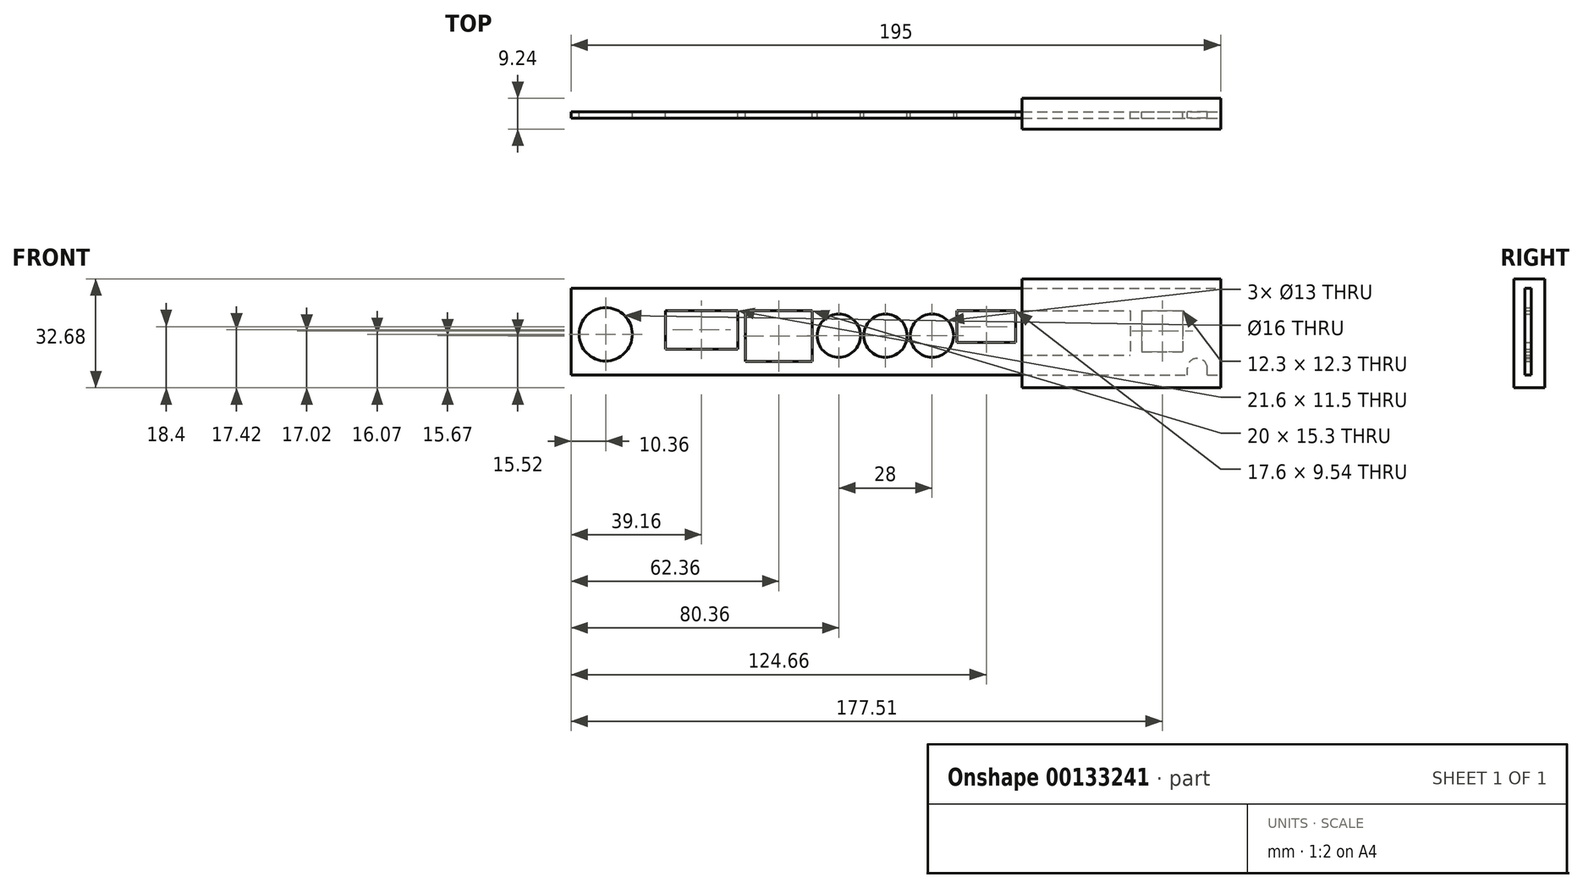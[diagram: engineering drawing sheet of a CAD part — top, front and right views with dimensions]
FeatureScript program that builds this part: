
annotation { "Feature Type Name" : "Feature", "Feature Type Description" : "" }
export const myFeature = defineFeature(function(context is Context, id is Id, definition is map)
    precondition{}
    {
        {
            var Q0;
            Q0=qCreatedBy(makeId("Front.planeOp"),FACE);
            var sketch = newSketch(context, id + "F0", { "sketchPlane" : qUnion([Q0])});
            skLineSegment(sketch, "E0.bottom", {"start": v(-97.5, 0) * mm, "end": v(97.5, 0) * mm});
            skLineSegment(sketch, "E0.top", {"start": v(-97.5, -26) * mm, "end": v(87.5, -26) * mm});
            skLineSegment(sketch, "E0.left", {"start": v(-97.5, 0) * mm, "end": v(-97.5, -26) * mm});
            skLineSegment(sketch, "E0.right", {"start": v(97.5, 0) * mm, "end": v(97.5, -26) * mm});
            skPoint(sketch, "E1", {"position": v(0, 0) * mm});
            skLineSegment(sketch, "E2", {"start": v(-87.14, -4.04) * mm, "end": v(-87.14, -25.05) * mm, "construction": true});
            skLineSegment(sketch, "E3", {"start": v(-100.2, -13.8) * mm, "end": v(-77.18, -13.8) * mm, "construction": true});
            skCircle(sketch, "E4", {"center": v(-87.14, -13.8) * mm, "radius": 8 * mm});
            skLineSegment(sketch, "E5.bottom", {"start": v(-69.14, -6.7) * mm, "end": v(-47.54, -6.7) * mm});
            skLineSegment(sketch, "E5.top", {"start": v(-69.14, -18.2) * mm, "end": v(-47.54, -18.2) * mm});
            skLineSegment(sketch, "E5.left", {"start": v(-69.14, -6.7) * mm, "end": v(-69.14, -18.2) * mm});
            skLineSegment(sketch, "E5.right", {"start": v(-47.54, -6.7) * mm, "end": v(-47.54, -18.2) * mm});
            skLineSegment(sketch, "E6.bottom", {"start": v(-45.14, -6.7) * mm, "end": v(-25.14, -6.7) * mm});
            skLineSegment(sketch, "E6.top", {"start": v(-45.14, -22) * mm, "end": v(-25.14, -22) * mm});
            skLineSegment(sketch, "E6.left", {"start": v(-45.14, -6.7) * mm, "end": v(-45.14, -22) * mm});
            skLineSegment(sketch, "E6.right", {"start": v(-25.14, -6.7) * mm, "end": v(-25.14, -22) * mm});
            skCircle(sketch, "E7", {"center": v(-17.14, -14.2) * mm, "radius": 6.5 * mm});
            skCircle(sketch, "E8.1.0.0", {"center": v(-3.14, -14.2) * mm, "radius": 6.5 * mm});
            skCircle(sketch, "E8.2.0.0", {"center": v(10.86, -14.2) * mm, "radius": 6.5 * mm});
            skLineSegment(sketch, "E8.direction1", {"start": v(-17.14, -14.2) * mm, "end": v(-3.14, -14.2) * mm, "construction": true});
            skLineSegment(sketch, "E9.bottom", {"start": v(18.36, -6.7) * mm, "end": v(35.96, -6.7) * mm});
            skLineSegment(sketch, "E9.top", {"start": v(18.36, -16.24) * mm, "end": v(35.96, -16.24) * mm});
            skLineSegment(sketch, "E9.left", {"start": v(18.36, -6.7) * mm, "end": v(18.36, -16.24) * mm});
            skLineSegment(sketch, "E9.right", {"start": v(35.96, -6.7) * mm, "end": v(35.96, -16.24) * mm});
            skLineSegment(sketch, "E10.bottom", {"start": v(37.86, -6.7) * mm, "end": v(70.36, -6.7) * mm});
            skLineSegment(sketch, "E10.top", {"start": v(37.86, -20.1) * mm, "end": v(70.36, -20.1) * mm});
            skLineSegment(sketch, "E10.left", {"start": v(37.86, -6.7) * mm, "end": v(37.86, -20.1) * mm});
            skLineSegment(sketch, "E10.right", {"start": v(70.36, -6.7) * mm, "end": v(70.36, -20.1) * mm});
            skLineSegment(sketch, "E11.bottom", {"start": v(73.86, -6.7) * mm, "end": v(86.16, -6.7) * mm});
            skLineSegment(sketch, "E11.top", {"start": v(73.86, -19) * mm, "end": v(86.16, -19) * mm});
            skLineSegment(sketch, "E11.left", {"start": v(73.86, -6.7) * mm, "end": v(73.86, -19) * mm});
            skLineSegment(sketch, "E11.right", {"start": v(86.16, -6.7) * mm, "end": v(86.16, -19) * mm});
            skLineSegment(sketch, "E12.top", {"start": v(90.5, -21) * mm, "end": v(90.5, -21) * mm});
            skLineSegment(sketch, "E12.left", {"start": v(87.5, -26) * mm, "end": v(87.5, -24) * mm});
            skLineSegment(sketch, "E12.right", {"start": v(93.5, -26) * mm, "end": v(93.5, -24) * mm});
            skPoint(sketch, "E13.visualSharp", {"position": v(87.5, -21) * mm});
            skArc(sketch, "E13.filletArc", {"start": v(90.5, -21) * mm, "mid": v(88.38, -21.88) * mm, "end": v(87.5, -24) * mm});
            skPoint(sketch, "E14.visualSharp", {"position": v(93.5, -21) * mm});
            skArc(sketch, "E14.filletArc", {"start": v(93.5, -24) * mm, "mid": v(92.62, -21.88) * mm, "end": v(90.5, -21) * mm});
            skLineSegment(sketch, "E15.trimOffspring", {"start": v(93.5, -26) * mm, "end": v(97.5, -26) * mm});
            skSolve(sketch);
        }
        {
            var Q0;
            Q0=makeQuery(id+"F0.imprint","IMPRINT",FACE,{"disambiguationData":[TD([[makeQuery(id+"F0.imprint","IMPRINT",EDGE,{"derivedFrom":sQuery(id+"F0.wireOp",EDGE,"E0.bottom")}),-1.0]])]});
            extrude(context, id + "F1", {"entities" : qUnion([Q0]), "depth" : 2 * mm});
        }
        {
            var Q0;
            Q0=makeQuery(id+"F1.opExtrude","SWEPT_FACE",FACE,{"disambiguationData":[OSD([sQuery(id+"F0.wireOp",EDGE,"E10.left")])]});
            cPlane(context, id + "F2", {"entities" : qUnion([Q0]), "cplaneType" : CPlaneType.OFFSET, "offset" : 0 * mm, "width" : 150 * mm, "height" : 150 * mm});
        }
        {
            var Q0;
            Q0=qCreatedBy(id+"F2.planeOp",FACE);
            var sketch = newSketch(context, id + "F3", { "sketchPlane" : qUnion([Q0])});
            skLineSegment(sketch, "E16.bottom", {"start": v(-5.21, -29.87) * mm, "end": v(4.03, -29.87) * mm});
            skLineSegment(sketch, "E16.top", {"start": v(-5.21, 2.8) * mm, "end": v(4.03, 2.8) * mm});
            skLineSegment(sketch, "E16.left", {"start": v(-5.21, -29.87) * mm, "end": v(-5.21, 2.8) * mm});
            skLineSegment(sketch, "E16.right", {"start": v(4.03, -29.87) * mm, "end": v(4.03, 2.8) * mm});
            skSolve(sketch);
        }
        {
            var Q0;
            Q0 = qSketchRegion(id + "F3", true);
            var Q1;
            Q1=makeQuery(id+"F1.opExtrude","SWEPT_FACE",FACE,{"disambiguationData":[OSD([sQuery(id+"F0.wireOp",EDGE,"E0.right")])]});
            extrude(context, id + "F4", {"entities" : qUnion([Q0]), "endBound" : BoundingType.UP_TO_SURFACE, "endBoundEntityFace" : qUnion([Q1]), "depth" : 39.23 * mm});
        }
        {
            var Q0;
            Q0=makeQuery(id+"F4.opExtrude","CAP_FACE",FACE,{"disambiguationData":[OSD([sQuery(id+"F3.wireOp",EDGE,"E16.bottom"),sQuery(id+"F3.wireOp",EDGE,"E16.top"),sQuery(id+"F3.wireOp",EDGE,"E16.left"),sQuery(id+"F3.wireOp",EDGE,"E16.right")])],"isStart":true});
            var Q1;
            Q1=makeQuery(id+"F1.opExtrude","SWEPT_FACE",FACE,{"disambiguationData":[OSD([sQuery(id+"F0.wireOp",EDGE,"E0.left")])]});
            extrude(context, id + "F5", {"entities" : qUnion([Q0]), "endBound" : BoundingType.UP_TO_SURFACE, "endBoundEntityFace" : qUnion([Q1]), "depth" : 25 * mm});
        }
        {
            var Q0;
            Q0=makeQuery(id+"F1.opExtrude","SWEPT_BODY",BODY,{"disambiguationData":[OSD([sQuery(id+"F0.wireOp",EDGE,"E0.bottom"),sQuery(id+"F0.wireOp",EDGE,"E0.top"),sQuery(id+"F0.wireOp",EDGE,"E0.left"),sQuery(id+"F0.wireOp",EDGE,"E0.right"),sQuery(id+"F0.wireOp",EDGE,"E4"),sQuery(id+"F0.wireOp",EDGE,"E5.bottom"),sQuery(id+"F0.wireOp",EDGE,"E5.top"),sQuery(id+"F0.wireOp",EDGE,"E5.left"),sQuery(id+"F0.wireOp",EDGE,"E5.right"),sQuery(id+"F0.wireOp",EDGE,"E6.bottom"),sQuery(id+"F0.wireOp",EDGE,"E6.top"),sQuery(id+"F0.wireOp",EDGE,"E6.left"),sQuery(id+"F0.wireOp",EDGE,"E6.right"),sQuery(id+"F0.wireOp",EDGE,"E7"),sQuery(id+"F0.wireOp",EDGE,"E8.1.0.0"),sQuery(id+"F0.wireOp",EDGE,"E8.2.0.0"),sQuery(id+"F0.wireOp",EDGE,"E9.bottom"),sQuery(id+"F0.wireOp",EDGE,"E9.top"),sQuery(id+"F0.wireOp",EDGE,"E9.left"),sQuery(id+"F0.wireOp",EDGE,"E9.right"),sQuery(id+"F0.wireOp",EDGE,"E10.bottom"),sQuery(id+"F0.wireOp",EDGE,"E10.top"),sQuery(id+"F0.wireOp",EDGE,"E10.left"),sQuery(id+"F0.wireOp",EDGE,"E10.right"),sQuery(id+"F0.wireOp",EDGE,"E11.bottom"),sQuery(id+"F0.wireOp",EDGE,"E11.top"),sQuery(id+"F0.wireOp",EDGE,"E11.left"),sQuery(id+"F0.wireOp",EDGE,"E11.right")])]});
            var Q1;
            Q1=makeQuery(id+"F4.opExtrude","SWEPT_BODY",BODY,{"disambiguationData":[OSD([sQuery(id+"F3.wireOp",EDGE,"E16.bottom"),sQuery(id+"F3.wireOp",EDGE,"E16.top"),sQuery(id+"F3.wireOp",EDGE,"E16.left"),sQuery(id+"F3.wireOp",EDGE,"E16.right")])]});
            booleanBodies(context, id + "F6", {"operationType" : BooleanOperationType.INTERSECTION, "tools" : qUnion([Q0, Q1]), "keepTools" : true});
        }
        {
            var Q0;
            Q0=makeQuery(id+"F5.opExtrude","SWEPT_BODY",BODY,{"disambiguationData":[OSD([sQuery(id+"F3.wireOp",EDGE,"E16.bottom"),sQuery(id+"F3.wireOp",EDGE,"E16.top"),sQuery(id+"F3.wireOp",EDGE,"E16.left"),sQuery(id+"F3.wireOp",EDGE,"E16.right")])]});
            var Q1;
            Q1=makeQuery(id+"F1.opExtrude","SWEPT_BODY",BODY,{"disambiguationData":[OSD([sQuery(id+"F0.wireOp",EDGE,"E0.bottom"),sQuery(id+"F0.wireOp",EDGE,"E0.top"),sQuery(id+"F0.wireOp",EDGE,"E0.left"),sQuery(id+"F0.wireOp",EDGE,"E0.right"),sQuery(id+"F0.wireOp",EDGE,"E4"),sQuery(id+"F0.wireOp",EDGE,"E5.bottom"),sQuery(id+"F0.wireOp",EDGE,"E5.top"),sQuery(id+"F0.wireOp",EDGE,"E5.left"),sQuery(id+"F0.wireOp",EDGE,"E5.right"),sQuery(id+"F0.wireOp",EDGE,"E6.bottom"),sQuery(id+"F0.wireOp",EDGE,"E6.top"),sQuery(id+"F0.wireOp",EDGE,"E6.left"),sQuery(id+"F0.wireOp",EDGE,"E6.right"),sQuery(id+"F0.wireOp",EDGE,"E7"),sQuery(id+"F0.wireOp",EDGE,"E8.1.0.0"),sQuery(id+"F0.wireOp",EDGE,"E8.2.0.0"),sQuery(id+"F0.wireOp",EDGE,"E9.bottom"),sQuery(id+"F0.wireOp",EDGE,"E9.top"),sQuery(id+"F0.wireOp",EDGE,"E9.left"),sQuery(id+"F0.wireOp",EDGE,"E9.right"),sQuery(id+"F0.wireOp",EDGE,"E10.bottom"),sQuery(id+"F0.wireOp",EDGE,"E10.top"),sQuery(id+"F0.wireOp",EDGE,"E10.left"),sQuery(id+"F0.wireOp",EDGE,"E10.right"),sQuery(id+"F0.wireOp",EDGE,"E11.bottom"),sQuery(id+"F0.wireOp",EDGE,"E11.top"),sQuery(id+"F0.wireOp",EDGE,"E11.left"),sQuery(id+"F0.wireOp",EDGE,"E11.right")])]});
            booleanBodies(context, id + "F7", {"operationType" : BooleanOperationType.INTERSECTION, "tools" : qUnion([Q0, Q1])});
        }
    });
